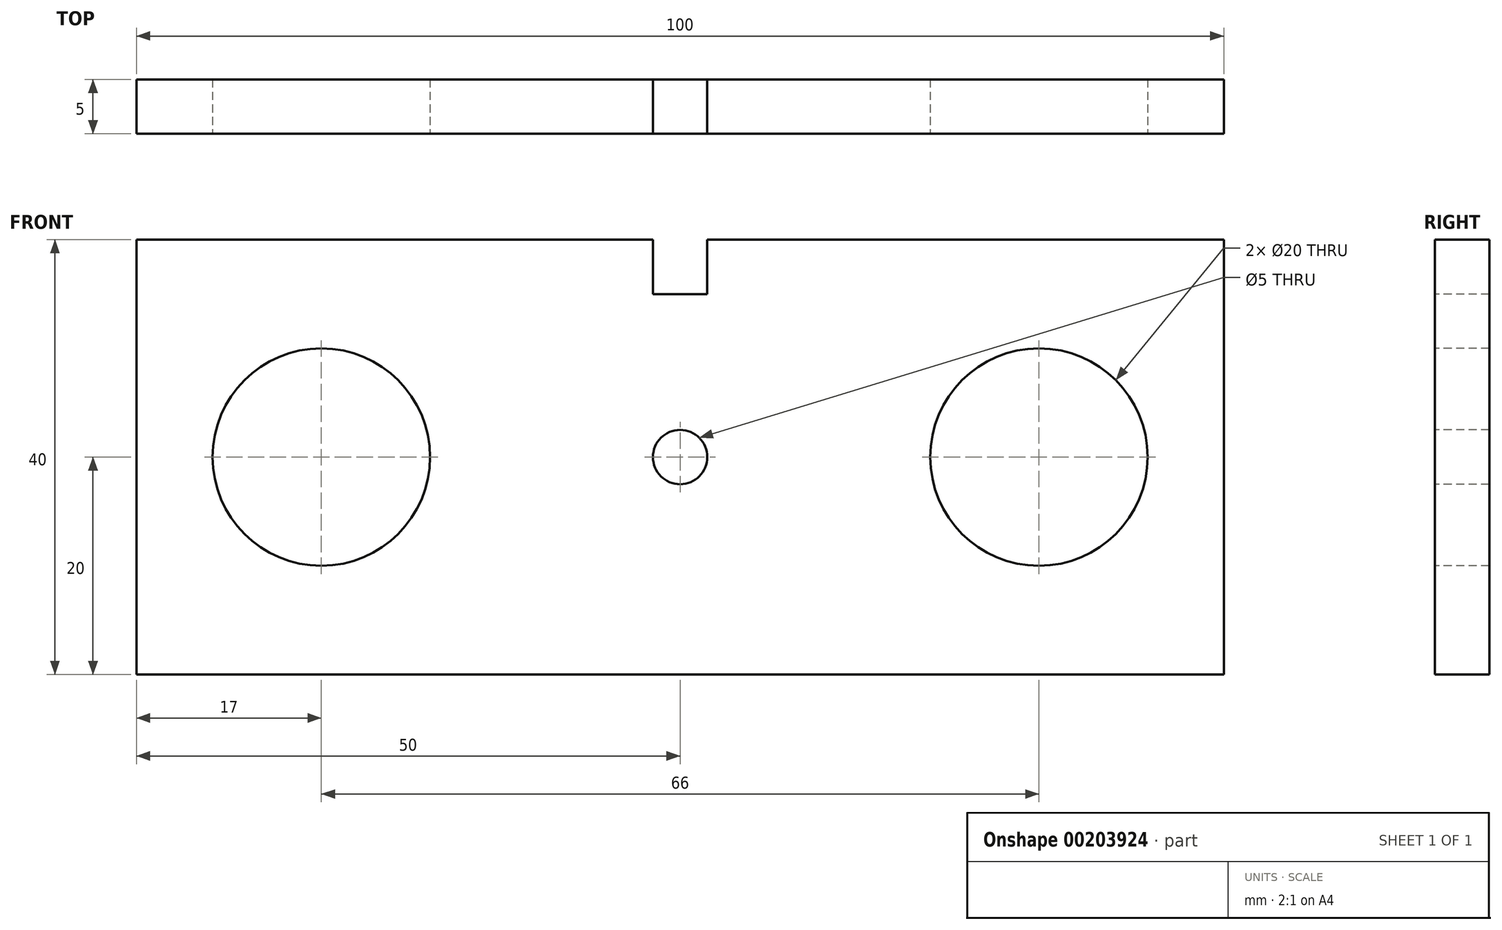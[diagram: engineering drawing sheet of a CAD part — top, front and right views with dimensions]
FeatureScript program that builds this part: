
annotation { "Feature Type Name" : "Feature", "Feature Type Description" : "" }
export const myFeature = defineFeature(function(context is Context, id is Id, definition is map)
    precondition{}
    {
        {
            var Q0;
            Q0=qCreatedBy(makeId("Front.planeOp"),FACE);
            var sketch = newSketch(context, id + "F0", { "sketchPlane" : qUnion([Q0])});
            skLineSegment(sketch, "E0.bottom", {"start": v(50, 20) * mm, "end": v(-50, 20) * mm});
            skLineSegment(sketch, "E0.top", {"start": v(50, -20) * mm, "end": v(-50, -20) * mm});
            skLineSegment(sketch, "E0.left", {"start": v(50, 20) * mm, "end": v(50, -20) * mm});
            skLineSegment(sketch, "E0.right", {"start": v(-50, 20) * mm, "end": v(-50, -20) * mm});
            skPoint(sketch, "E0.middle", {"position": v(0, 0) * mm});
            skSolve(sketch);
        }
        {
            var Q0;
            Q0=qSketchRegion(id+"F0",true);
            extrude(context, id + "F1", {"entities" : qUnion([Q0]), "depth" : 5 * mm});
        }
        {
            var Q0;
            Q0=makeQuery(id+"F1.opExtrude","CAP_FACE",FACE,{"disambiguationData":[OSD([sQuery(id+"F0.wireOp",EDGE,"E0.bottom"),sQuery(id+"F0.wireOp",EDGE,"E0.top"),sQuery(id+"F0.wireOp",EDGE,"E0.left"),sQuery(id+"F0.wireOp",EDGE,"E0.right")])],"isStart":false});
            var sketch = newSketch(context, id + "F2", { "sketchPlane" : qUnion([Q0])});
            skLineSegment(sketch, "E1", {"start": v(-24.95, 0) * mm, "end": v(24.45, 0) * mm, "construction": true});
            skCircle(sketch, "E2", {"center": v(-33, 0) * mm, "radius": 10 * mm});
            skCircle(sketch, "E3", {"center": v(0, 0) * mm, "radius": 2.5 * mm});
            skCircle(sketch, "E4", {"center": v(33, 0) * mm, "radius": 10 * mm});
            skSolve(sketch);
        }
        {
            var Q0;
            Q0=qSketchRegion(id+"F2",true);
            extrude(context, id + "F3", {"entities" : qUnion([Q0]), "operationType" : NewBodyOperationType.REMOVE, "endBound" : BoundingType.UP_TO_NEXT, "oppositeDirection" : true, "depth" : 25 * mm});
        }
        {
            var Q0;
            Q0=makeQuery(id+"F1.opExtrude","CAP_FACE",FACE,{"disambiguationData":[OSD([sQuery(id+"F0.wireOp",EDGE,"E0.bottom"),sQuery(id+"F0.wireOp",EDGE,"E0.top"),sQuery(id+"F0.wireOp",EDGE,"E0.left"),sQuery(id+"F0.wireOp",EDGE,"E0.right")])],"isStart":false});
            var sketch = newSketch(context, id + "F4", { "sketchPlane" : qUnion([Q0])});
            skLineSegment(sketch, "E5", {"start": v(0, 0) * mm, "end": v(0, 20) * mm, "construction": true});
            skLineSegment(sketch, "E6", {"start": v(-2.5, 20) * mm, "end": v(-2.5, 15) * mm});
            skLineSegment(sketch, "E7", {"start": v(-2.5, 15) * mm, "end": v(2.5, 15) * mm});
            skLineSegment(sketch, "E8", {"start": v(2.5, 15) * mm, "end": v(2.5, 20) * mm});
            skLineSegment(sketch, "E9", {"start": v(2.5, 20) * mm, "end": v(-2.5, 20) * mm});
            skSolve(sketch);
        }
        {
            var Q0;
            Q0=qSketchRegion(id+"F4",true);
            extrude(context, id + "F5", {"entities" : qUnion([Q0]), "operationType" : NewBodyOperationType.REMOVE, "endBound" : BoundingType.UP_TO_NEXT, "oppositeDirection" : true, "depth" : 25 * mm});
        }
    });
